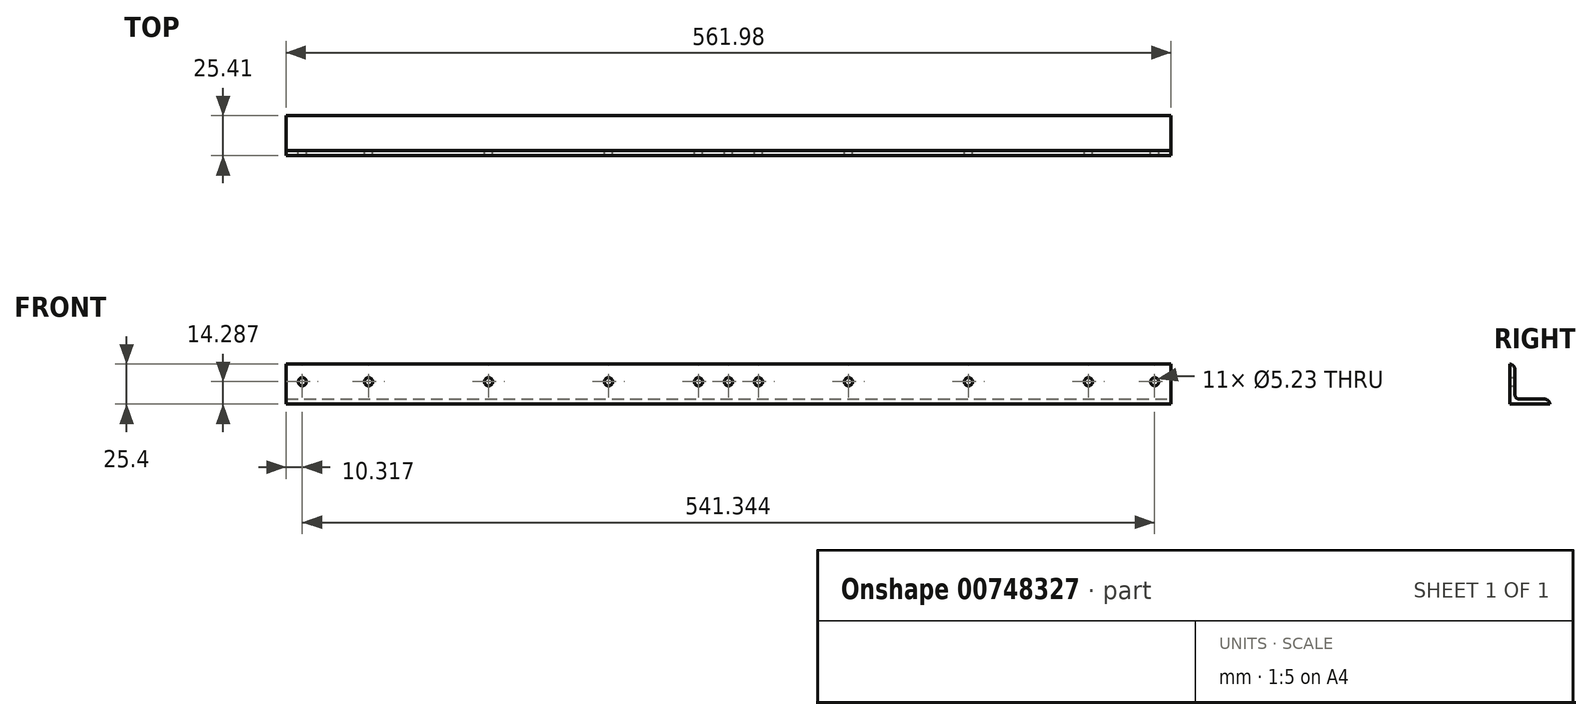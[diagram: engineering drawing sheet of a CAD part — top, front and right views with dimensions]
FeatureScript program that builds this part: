
annotation { "Feature Type Name" : "Feature", "Feature Type Description" : "" }
export const myFeature = defineFeature(function(context is Context, id is Id, definition is map)
    precondition{}
    {
        {
            var Q0;
            Q0=qCreatedBy(makeId("Right.planeOp"),FACE);
            var sketch = newSketch(context, id + "F0", { "sketchPlane" : qUnion([Q0])});
            skLineSegment(sketch, "E0", {"start": v(0, -3.18) * mm, "end": v(0, -19.05) * mm});
            skLineSegment(sketch, "E1", {"start": v(3.18, -22.23) * mm, "end": v(19.05, -22.22) * mm});
            skLineSegment(sketch, "E2.0", {"start": v(-3.17, -25.4) * mm, "end": v(22.23, -25.4) * mm});
            skLineSegment(sketch, "E2.1", {"start": v(-3.17, 0) * mm, "end": v(-3.18, -25.4) * mm});
            skLineSegment(sketch, "E3", {"start": v(-3.18, 0) * mm, "end": v(-3.18, 0) * mm});
            skLineSegment(sketch, "E4", {"start": v(22.23, -25.4) * mm, "end": v(22.23, -25.4) * mm});
            skPoint(sketch, "E5.visualSharp", {"position": v(0, -22.23) * mm});
            skArc(sketch, "E5.filletArc", {"start": v(0, -19.05) * mm, "mid": v(0.93, -21.3) * mm, "end": v(3.18, -22.23) * mm});
            skPoint(sketch, "E6.visualSharp", {"position": v(22.23, -22.22) * mm});
            skArc(sketch, "E6.filletArc", {"start": v(22.23, -25.4) * mm, "mid": v(21.3, -23.15) * mm, "end": v(19.05, -22.22) * mm});
            skPoint(sketch, "E7.visualSharp", {"position": v(0, 0) * mm});
            skArc(sketch, "E7.filletArc", {"start": v(0, -3.18) * mm, "mid": v(-0.93, -0.93) * mm, "end": v(-3.18, 0) * mm});
            skSolve(sketch);
        }
        {
            var Q0;
            Q0=makeQuery(id+"F0.imprint","IMPRINT",FACE,{"disambiguationData":[TD([[makeQuery(id+"F0.imprint","IMPRINT",EDGE,{"derivedFrom":sQuery(id+"F0.wireOp",EDGE,"E0")}),-1.0]])]});
            extrude(context, id + "F1", {"entities" : qUnion([Q0]), "oppositeDirection" : true, "depth" : 561.98 * mm, "offsetDistance" : 25.4 * mm});
        }
        {
            var Q0;
            Q0=makeQuery(id+"F1.opExtrude","SWEPT_FACE",FACE,{"disambiguationData":[OSD([sQuery(id+"F0.wireOp",EDGE,"E0")])]});
            var sketch = newSketch(context, id + "F2", { "sketchPlane" : qUnion([Q0])});
            skCircle(sketch, "E8", {"center": v(10.32, -11.11) * mm, "radius": 2.62 * mm});
            skCircle(sketch, "E9", {"center": v(280.99, -11.11) * mm, "radius": 2.62 * mm});
            skCircle(sketch, "E10", {"center": v(551.66, -11.11) * mm, "radius": 2.62 * mm});
            skCircle(sketch, "E11", {"center": v(128.59, -11.11) * mm, "radius": 2.62 * mm});
            skCircle(sketch, "E12", {"center": v(204.79, -11.11) * mm, "radius": 2.62 * mm});
            skCircle(sketch, "E13", {"center": v(357.19, -11.11) * mm, "radius": 2.62 * mm});
            skCircle(sketch, "E14", {"center": v(433.39, -11.11) * mm, "radius": 2.62 * mm});
            skCircle(sketch, "E15", {"center": v(509.59, -11.11) * mm, "radius": 2.62 * mm});
            skCircle(sketch, "E16", {"center": v(52.39, -11.11) * mm, "radius": 2.62 * mm});
            skCircle(sketch, "E17", {"center": v(261.94, -11.11) * mm, "radius": 2.62 * mm});
            skCircle(sketch, "E18", {"center": v(300.04, -11.11) * mm, "radius": 2.62 * mm});
            skLineSegment(sketch, "E19", {"start": v(280.99, -3.18) * mm, "end": v(280.99, -19.05) * mm, "construction": true});
            skLineSegment(sketch, "E20.0", {"start": v(204.79, -3.18) * mm, "end": v(204.79, -12.7) * mm, "construction": true});
            skLineSegment(sketch, "E21.0", {"start": v(128.59, -3.18) * mm, "end": v(128.59, -12.7) * mm, "construction": true});
            skLineSegment(sketch, "E22.0", {"start": v(52.39, -3.18) * mm, "end": v(52.39, -12.7) * mm, "construction": true});
            skLineSegment(sketch, "E23.0", {"start": v(357.19, -3.18) * mm, "end": v(357.19, -12.7) * mm, "construction": true});
            skLineSegment(sketch, "E24.0", {"start": v(433.39, -3.18) * mm, "end": v(433.39, -12.7) * mm, "construction": true});
            skLineSegment(sketch, "E25.0", {"start": v(509.59, -3.18) * mm, "end": v(509.59, -12.7) * mm, "construction": true});
            skLineSegment(sketch, "E26", {"start": v(561.98, -11.11) * mm, "end": v(0, -11.11) * mm, "construction": true});
            skSolve(sketch);
        }
        {
            var Q0;
            Q0=qSketchRegion(id+"F2",true);
            extrude(context, id + "F3", {"entities" : qUnion([Q0]), "operationType" : NewBodyOperationType.REMOVE, "oppositeDirection" : true, "depth" : 25.4 * mm, "offsetDistance" : 25.4 * mm});
        }
    });
